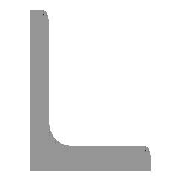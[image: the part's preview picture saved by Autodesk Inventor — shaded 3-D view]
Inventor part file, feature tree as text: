
AUTODESK INVENTOR PART (.ipt)
format: ipt  version: 2013 (Build 170138000, 138)  size: 129,024 bytes
history: native  units: mm (DEFAULTED — no unit token found)
features: other x4, plane x3, split x2, sketch x2
ambient origin geometry x8: Origin, YZ Plane, XZ Plane, XY Plane, X Axis, Y Axis, Z Axis, Center Point
bodies: Solid1 (feature_tree), Body (feature_tree)
feature tree (11):
  parser-record x1  (decoder bookkeeping rows leaked as tree rows — omitted from the tree; the rows remain in map.json)
  other  "Driven Length"
  other  "Start plane"
  other  "End plane"
  plane  "Work Plane4"
  split  "Split1"
  plane  "Work Plane5"
  split  "Split2"
  sketch  "Sketch3"  dims[d0=38.1mm]
  plane  "Work Plane3"
  sketch  "Sketch4"  dims[d1=38.1mm d2=4.7625mm d3=4.7625mm d4=558.8mm d5=0.0mm d10=0.0mm d11=0.0mm d12=-0.0mm d13=558.8mm d14=4.826mm d15=2.286mm d16=90.0deg d17=558.8mm]
